# Revit family: 820-00-024 DN125-150
name_source: partatom
category: Pipe Accessories
units: mm (PartAtom-declared; Revit-internal decimal feet)

## family parameters
Always vertical = Yes
Cut with Voids When Loaded = No
Part Type = Valve - Breaks Into
Round Connector Dimension = Use Diameter
Shared = No
Work Plane-Based = No

## types (2) — shared parameters
1 = 1 mm  [stored 0.00328084 ft]
90 = 90 mm  [stored 0.295276 ft]
Body_wallthickness = 10 mm  [stored 0.0328084 ft]
DN125_PN10/16 = 820-0125-00-521L0160002
DN150_PN10/16 = 820-0150-00-521L0160002
Description_ = AVK CENTRIC BUTTERFLY VALVE WAFER TYPE, PN10/16
F = 14 mm  [stored 0.0459318 ft]
F2 = 16 mm  [stored 0.0524934 ft]
FL_T = 15 mm  [stored 0.0492126 ft]
Fillet = 19 mm  [stored 0.062336 ft]
Flange_thickness = 9 mm  [stored 0.0295276 ft]
Hole_dia = 19 mm  [stored 0.062336 ft]
L = 56 mm  [stored 0.183727 ft]
L-2 = 54 mm  [stored 0.177165 ft]
LUG_T = 27 mm  [stored 0.0885827 ft]
L_ref = 36 mm  [stored 0.11811 ft]
L_ref_2 = 72 mm  [stored 0.23622 ft]
L_ref_3 = 30 mm  [stored 0.0984252 ft]
Lug_D = 13 mm  [stored 0.0426509 ft]
Search_table = 820-00-024 DN125-150
URL product pages = https://www.avkvalves.com
disk = 20 mm  [stored 0.0656168 ft]
fillet = 20 mm  [stored 0.0656168 ft]
zero-valued in all types: Default Elevation

## per-type parameters (varying)
| type | Actuator_Dia | Bore | DN | EPDM | EPDM_R | FL_R | H2 | Hole_L | Hole_L1 | ID | L2 | PCD | W2_ref | Wafer_dim | Wafer_dim1 |
| DN125_PN10/16 | 65 mm  [stored 0.213255 ft] | 63 mm  [stored 0.206693 ft] | 125 mm  [stored 0.410105 ft] | 62 mm | 81 mm | 73 mm | 128 mm  [stored 0.419948 ft] | 45 mm  [stored 0.147638 ft] | 109 mm | 63 mm  [stored 0.206693 ft] | 91 mm | 105 mm  [stored 0.344488 ft] | 195 mm | 54 mm  [stored 0.177165 ft] | 122 mm |
| DN150_PN10/16 | 90 mm  [stored 0.295276 ft] | 75 mm | 150 mm  [stored 0.492126 ft] | 74 mm  [stored 0.242782 ft] | 92 mm  [stored 0.301837 ft] | 85 mm  [stored 0.278871 ft] | 141 mm  [stored 0.462598 ft] | 51 mm  [stored 0.167323 ft] | 123 mm  [stored 0.403543 ft] | 75 mm | 103 mm | 120 mm  [stored 0.393701 ft] | 210 mm | 62 mm | 138 mm  [stored 0.452756 ft] |

note: [stored X ft] marks values corroborated as IEEE doubles in the binary element streams (Revit-internal decimal feet)

## geometry (parser evidence)
native form markers: Sweep x4
no freeform markers — native parametric forms only
